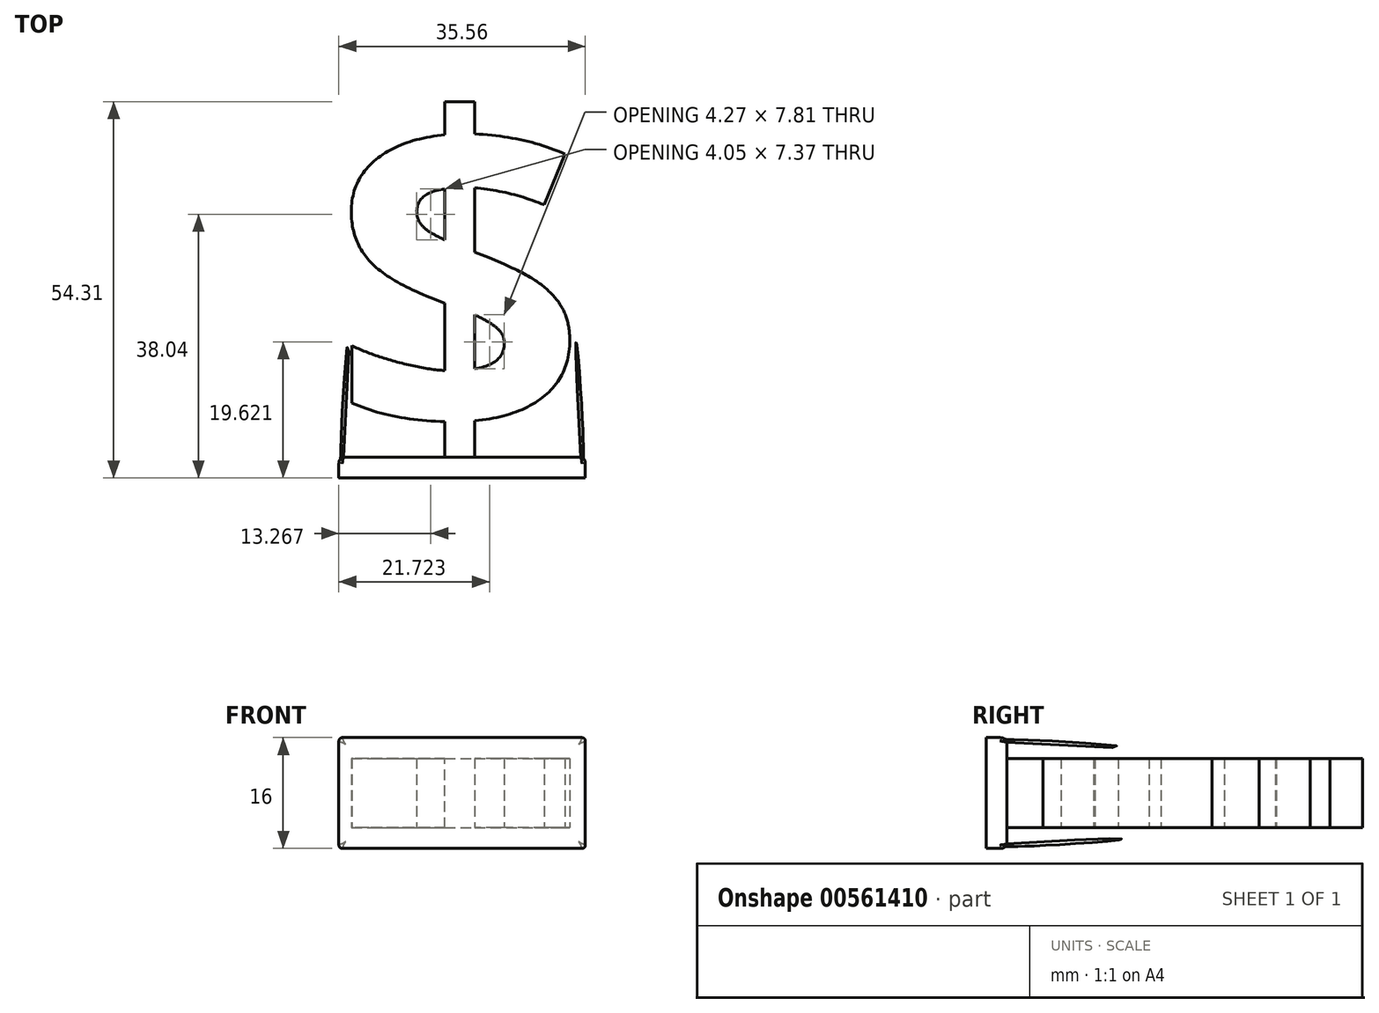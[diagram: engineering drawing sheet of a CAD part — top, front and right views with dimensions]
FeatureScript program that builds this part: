
annotation { "Feature Type Name" : "Feature", "Feature Type Description" : "" }
export const myFeature = defineFeature(function(context is Context, id is Id, definition is map)
    precondition{}
    {
        {
            var Q0;
            Q0=qCreatedBy(makeId("Top.planeOp"),FACE);
            var sketch = newSketch(context, id + "F0", { "sketchPlane" : qUnion([Q0])});
            skText(sketch, "E0", { "text": "$", "fontName": "OpenSans-Bold.ttf"});
            const initialGuessF0  = {"E0": [-0.02193, 0.00554, 1, 0, 0.04628]};
            skSetInitialGuess(sketch, initialGuessF0);
            skSolve(sketch);
        }
        {
            var Q0;
            Q0 = qSketchRegion(id + "F0", true);
            extrude(context, id + "F1", {"entities" : qUnion([Q0]), "depth" : 10 * mm, "offsetDistance" : 25 * mm});
        }
        {
            var Q0;
            Q0=qCreatedBy(makeId("Front.planeOp"),FACE);
            var sketch = newSketch(context, id + "F2", { "sketchPlane" : qUnion([Q0])});
            skLineSegment(sketch, "E1.bottom", {"start": v(14.6, 13) * mm, "end": v(-20.96, 13) * mm});
            skLineSegment(sketch, "E1.top", {"start": v(14.6, -3) * mm, "end": v(-20.96, -3) * mm});
            skLineSegment(sketch, "E1.left", {"start": v(14.6, 13) * mm, "end": v(14.6, -3) * mm});
            skLineSegment(sketch, "E1.right", {"start": v(-20.96, 13) * mm, "end": v(-20.96, -3) * mm});
            skPoint(sketch, "E2", {"position": v(14.6, 0) * mm});
            skPoint(sketch, "E3", {"position": v(14.6, 10) * mm});
            skPoint(sketch, "E4", {"position": v(-19.11, 13) * mm});
            skSolve(sketch);
        }
        {
            var Q0;
            Q0 = qSketchRegion(id + "F2", true);
            extrude(context, id + "F3", {"entities" : qUnion([Q0]), "operationType" : NewBodyOperationType.ADD, "oppositeDirection" : true, "depth" : 3 * mm, "offsetDistance" : 25 * mm});
        }
        {
            var Q0;
            Q0=makeQuery(id+"F3.opExtrude","CAP_EDGE",EDGE,{"disambiguationData":[OSD([sQuery(id+"F2.wireOp",EDGE,"E1.left")])],"isStart":false});
            var Q1;
            Q1=makeQuery(id+"F3.opExtrude","CAP_EDGE",EDGE,{"disambiguationData":[OSD([sQuery(id+"F2.wireOp",EDGE,"E1.right")])],"isStart":false});
            var Q2;
            Q2=makeQuery(id+"F3.opExtrude","CAP_EDGE",EDGE,{"disambiguationData":[OSD([sQuery(id+"F2.wireOp",EDGE,"E1.top")])],"isStart":false});
            var Q3;
            Q3=makeQuery(id+"F3.opExtrude","CAP_EDGE",EDGE,{"disambiguationData":[OSD([sQuery(id+"F2.wireOp",EDGE,"E1.bottom")])],"isStart":false});
            fillet(context, id + "F4", {"entities" : qUnion([Q0, Q1, Q2, Q3]), "radius" : 1 * mm, "tangentPropagation" : true, "rho" : 0.5, "crossSection" : FilletCrossSection.CONIC, "allowEdgeOverflow" : false});
        }
        {
            var Q0;
            Q0=makeQuery(id+"F4.opFillet","BLEND_EDGE",EDGE,{"blendedFrom":[makeQuery(id+"F3.opExtrude","CAP_EDGE",EDGE,{"disambiguationData":[OSD([sQuery(id+"F2.wireOp",EDGE,"E1.top")])],"isStart":false}),makeQuery(id+"F3.opExtrude","CAP_EDGE",EDGE,{"disambiguationData":[OSD([sQuery(id+"F2.wireOp",EDGE,"E1.left")])],"isStart":false})],"blendedInto":[]});
            var Q1;
            Q1=makeQuery(id+"F3.opExtrude","SWEPT_EDGE",EDGE,{"disambiguationData":[OSD([sQuery(id+"F2.wireOp",EDGE,"E1.top"),sQuery(id+"F2.wireOp",EDGE,"E1.left")])]});
            var Q2;
            Q2=makeQuery(id+"F3.opExtrude","SWEPT_EDGE",EDGE,{"disambiguationData":[OSD([sQuery(id+"F2.wireOp",EDGE,"E1.bottom"),sQuery(id+"F2.wireOp",EDGE,"E1.left")])]});
            var Q3;
            Q3=makeQuery(id+"F4.opFillet","BLEND_EDGE",EDGE,{"blendedFrom":[makeQuery(id+"F3.opExtrude","CAP_EDGE",EDGE,{"disambiguationData":[OSD([sQuery(id+"F2.wireOp",EDGE,"E1.bottom")])],"isStart":false}),makeQuery(id+"F3.opExtrude","CAP_EDGE",EDGE,{"disambiguationData":[OSD([sQuery(id+"F2.wireOp",EDGE,"E1.left")])],"isStart":false})],"blendedInto":[]});
            var Q4;
            Q4=makeQuery(id+"F4.opFillet","BLEND_EDGE",EDGE,{"blendedFrom":[makeQuery(id+"F3.opExtrude","CAP_EDGE",EDGE,{"disambiguationData":[OSD([sQuery(id+"F2.wireOp",EDGE,"E1.top")])],"isStart":false}),makeQuery(id+"F3.opExtrude","CAP_EDGE",EDGE,{"disambiguationData":[OSD([sQuery(id+"F2.wireOp",EDGE,"E1.right")])],"isStart":false})],"blendedInto":[]});
            var Q5;
            Q5=makeQuery(id+"F3.opExtrude","SWEPT_EDGE",EDGE,{"disambiguationData":[OSD([sQuery(id+"F2.wireOp",EDGE,"E1.top"),sQuery(id+"F2.wireOp",EDGE,"E1.right")])]});
            var Q6;
            Q6=makeQuery(id+"F3.opExtrude","SWEPT_EDGE",EDGE,{"disambiguationData":[OSD([sQuery(id+"F2.wireOp",EDGE,"E1.bottom"),sQuery(id+"F2.wireOp",EDGE,"E1.right")])]});
            var Q7;
            Q7=makeQuery(id+"F4.opFillet","BLEND_EDGE",EDGE,{"blendedFrom":[makeQuery(id+"F3.opExtrude","CAP_EDGE",EDGE,{"disambiguationData":[OSD([sQuery(id+"F2.wireOp",EDGE,"E1.bottom")])],"isStart":false}),makeQuery(id+"F3.opExtrude","CAP_EDGE",EDGE,{"disambiguationData":[OSD([sQuery(id+"F2.wireOp",EDGE,"E1.right")])],"isStart":false})],"blendedInto":[]});
            fillet(context, id + "F5", {"entities" : qUnion([Q0, Q1, Q2, Q3, Q4, Q5, Q6, Q7]), "radius" : 0.5 * mm, "tangentPropagation" : true, "allowEdgeOverflow" : false});
        }
    });
